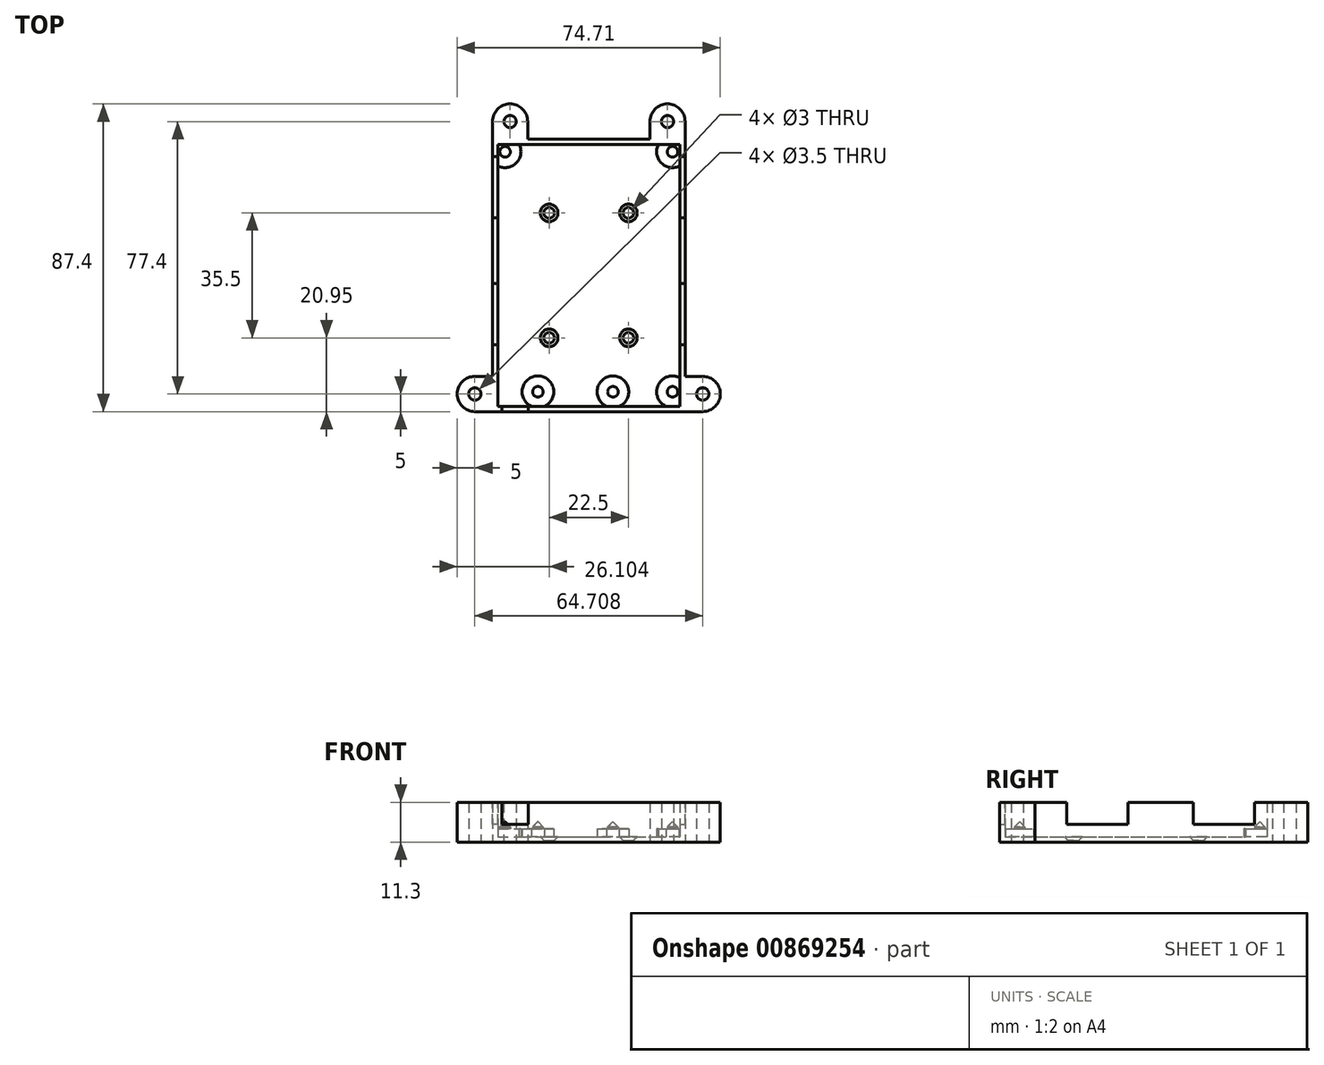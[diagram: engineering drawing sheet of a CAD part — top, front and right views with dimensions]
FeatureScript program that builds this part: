
annotation { "Feature Type Name" : "Feature", "Feature Type Description" : "" }
export const myFeature = defineFeature(function(context is Context, id is Id, definition is map)
    precondition{}
    {
        {
            var Q0;
            Q0=qCreatedBy(makeId("Top.planeOp"),FACE);
            var sketch = newSketch(context, id + "F0", { "sketchPlane" : qUnion([Q0])});
            skLineSegment(sketch, "E0.bottom", {"start": v(0, 0) * mm, "end": v(51.3, 0) * mm});
            skLineSegment(sketch, "E0.top", {"start": v(0, 74) * mm, "end": v(51.3, 74) * mm});
            skLineSegment(sketch, "E0.left", {"start": v(0, 0) * mm, "end": v(0, 74) * mm});
            skLineSegment(sketch, "E0.right", {"start": v(51.3, 0) * mm, "end": v(51.3, 74) * mm});
            skLineSegment(sketch, "E1.bottom", {"start": v(0, 69) * mm, "end": v(16.7, 69) * mm, "construction": true});
            skLineSegment(sketch, "E1.top", {"start": v(0, 55) * mm, "end": v(16.7, 55) * mm, "construction": true});
            skLineSegment(sketch, "E1.left", {"start": v(0, 69) * mm, "end": v(0, 55) * mm, "construction": true});
            skLineSegment(sketch, "E1.right", {"start": v(16.7, 69) * mm, "end": v(16.7, 55) * mm, "construction": true});
            skLineSegment(sketch, "E2.bottom", {"start": v(0, 33) * mm, "end": v(16.7, 33) * mm, "construction": true});
            skLineSegment(sketch, "E2.top", {"start": v(0, 19) * mm, "end": v(16.7, 19) * mm, "construction": true});
            skLineSegment(sketch, "E2.left", {"start": v(0, 33) * mm, "end": v(0, 19) * mm, "construction": true});
            skLineSegment(sketch, "E2.right", {"start": v(16.7, 33) * mm, "end": v(16.7, 19) * mm, "construction": true});
            skLineSegment(sketch, "E3.bottom", {"start": v(51.3, 69) * mm, "end": v(34.6, 69) * mm, "construction": true});
            skLineSegment(sketch, "E3.top", {"start": v(51.3, 55) * mm, "end": v(34.6, 55) * mm, "construction": true});
            skLineSegment(sketch, "E3.left", {"start": v(51.3, 69) * mm, "end": v(51.3, 55) * mm, "construction": true});
            skLineSegment(sketch, "E3.right", {"start": v(34.6, 69) * mm, "end": v(34.6, 55) * mm, "construction": true});
            skLineSegment(sketch, "E4.bottom", {"start": v(51.3, 33) * mm, "end": v(34.6, 33) * mm, "construction": true});
            skLineSegment(sketch, "E4.top", {"start": v(51.3, 19) * mm, "end": v(34.6, 19) * mm, "construction": true});
            skLineSegment(sketch, "E4.left", {"start": v(51.3, 33) * mm, "end": v(51.3, 19) * mm, "construction": true});
            skLineSegment(sketch, "E4.right", {"start": v(34.6, 33) * mm, "end": v(34.6, 19) * mm, "construction": true});
            skCircle(sketch, "E5", {"center": v(11.21, 3.92) * mm, "radius": 1.6 * mm});
            skCircle(sketch, "E6", {"center": v(32.51, 3.92) * mm, "radius": 1.6 * mm});
            skCircle(sketch, "E7", {"center": v(49.43, 3.92) * mm, "radius": 1.6 * mm});
            skCircle(sketch, "E8", {"center": v(49.43, 72.12) * mm, "radius": 1.6 * mm});
            skCircle(sketch, "E9", {"center": v(1.88, 72.12) * mm, "radius": 1.6 * mm});
            skLineSegment(sketch, "E10", {"start": v(1.88, 72.12) * mm, "end": v(49.43, 72.12) * mm, "construction": true});
            skSolve(sketch);
        }
        {
            var Q0;
            {var subQ10=sQuery(id+"F0.wireOp",EDGE,"E0.bottom");Q0=makeQuery(id+"F0.imprint","IMPRINT",FACE,{"disambiguationData":[TD([[makeQuery(id+"F0.imprint","IMPRINT",EDGE,{"derivedFrom":subQ10}),1.0]])]});}
            var sketch = newSketch(context, id + "F1", { "sketchPlane" : qUnion([Q0])});
            skLineSegment(sketch, "E11.0", {"start": v(-1.7, -1.7) * mm, "end": v(-1.7, 75.7) * mm});
            skLineSegment(sketch, "E11.1", {"start": v(-1.7, -1.7) * mm, "end": v(53, -1.7) * mm});
            skLineSegment(sketch, "E11.2", {"start": v(53, -1.7) * mm, "end": v(53, 75.7) * mm});
            skLineSegment(sketch, "E11.3", {"start": v(-1.7, 75.7) * mm, "end": v(53, 75.7) * mm});
            skSolve(sketch);
        }
        {
            var Q0;
            Q0=qSketchRegion(id+"F1",true);
            extrude(context, id + "F2", {"entities" : qUnion([Q0]), "depth" : 11.3 * mm, "offsetDistance" : 25 * mm});
        }
        {
            var Q0;
            Q0=makeQuery(id+"F2.opExtrude","CAP_FACE",FACE,{"disambiguationData":[OSD([sQuery(id+"F1.wireOp",EDGE,"E11.0"),sQuery(id+"F1.wireOp",EDGE,"E11.1"),sQuery(id+"F1.wireOp",EDGE,"E11.2"),sQuery(id+"F1.wireOp",EDGE,"E11.3")])],"isStart":false});
            shell(context, id + "F3", {"entities" : qUnion([Q0]), "thickness" : 1.5 * mm});
        }
        {
            var Q0;
            Q0=makeQuery(id+"F2.opExtrude","CAP_FACE",FACE,{"disambiguationData":[OSD([sQuery(id+"F1.wireOp",EDGE,"E11.0"),sQuery(id+"F1.wireOp",EDGE,"E11.1"),sQuery(id+"F1.wireOp",EDGE,"E11.2"),sQuery(id+"F1.wireOp",EDGE,"E11.3")])],"isStart":false});
            var sketch = newSketch(context, id + "F4", { "sketchPlane" : qUnion([Q0])});
            skLineSegment(sketch, "E12.0", {"start": v(16.7, 33) * mm, "end": v(16.7, 19) * mm, "construction": true});
            skLineSegment(sketch, "E13.0", {"start": v(34.6, 33) * mm, "end": v(34.6, 19) * mm, "construction": true});
            skLineSegment(sketch, "E14.0", {"start": v(16.7, 69) * mm, "end": v(16.7, 55) * mm, "construction": true});
            skLineSegment(sketch, "E15.0", {"start": v(34.6, 69) * mm, "end": v(34.6, 55) * mm, "construction": true});
            skLineSegment(sketch, "E16.0", {"start": v(0, 33) * mm, "end": v(16.7, 33) * mm, "construction": true});
            skLineSegment(sketch, "E17.0", {"start": v(0, 19) * mm, "end": v(16.7, 19) * mm, "construction": true});
            skLineSegment(sketch, "E18.0", {"start": v(51.3, 33) * mm, "end": v(34.6, 33) * mm, "construction": true});
            skLineSegment(sketch, "E19.0", {"start": v(51.3, 19) * mm, "end": v(34.6, 19) * mm, "construction": true});
            skLineSegment(sketch, "E20.0", {"start": v(51.3, 55) * mm, "end": v(34.6, 55) * mm, "construction": true});
            skLineSegment(sketch, "E21.0", {"start": v(51.3, 69) * mm, "end": v(34.6, 69) * mm, "construction": true});
            skLineSegment(sketch, "E22.0", {"start": v(0, 55) * mm, "end": v(16.7, 55) * mm, "construction": true});
            skLineSegment(sketch, "E23.0", {"start": v(0, 69) * mm, "end": v(16.7, 69) * mm, "construction": true});
            skLineSegment(sketch, "E24.0", {"start": v(0, 33) * mm, "end": v(0, 19) * mm});
            skLineSegment(sketch, "E25.0", {"start": v(51.3, 33) * mm, "end": v(51.3, 19) * mm});
            skLineSegment(sketch, "E26.0", {"start": v(0, 69) * mm, "end": v(0, 55) * mm});
            skLineSegment(sketch, "E27.0", {"start": v(51.3, 69) * mm, "end": v(51.3, 55) * mm});
            skLineSegment(sketch, "E28.0", {"start": v(-1.7, 17.3) * mm, "end": v(18.4, 17.3) * mm});
            skLineSegment(sketch, "E28.1", {"start": v(-1.7, 34.7) * mm, "end": v(-1.7, 17.3) * mm});
            skLineSegment(sketch, "E28.2", {"start": v(-1.7, 34.7) * mm, "end": v(18.4, 34.7) * mm});
            skLineSegment(sketch, "E28.3", {"start": v(18.4, 34.7) * mm, "end": v(18.4, 17.3) * mm});
            skLineSegment(sketch, "E29.0", {"start": v(53, 17.3) * mm, "end": v(32.9, 17.3) * mm});
            skLineSegment(sketch, "E29.1", {"start": v(53, 34.7) * mm, "end": v(53, 17.3) * mm});
            skLineSegment(sketch, "E29.2", {"start": v(53, 34.7) * mm, "end": v(32.9, 34.7) * mm});
            skLineSegment(sketch, "E29.3", {"start": v(32.9, 34.7) * mm, "end": v(32.9, 17.3) * mm});
            skLineSegment(sketch, "E30.0", {"start": v(-1.7, 53.3) * mm, "end": v(18.4, 53.3) * mm});
            skLineSegment(sketch, "E30.1", {"start": v(-1.7, 70.7) * mm, "end": v(-1.7, 53.3) * mm});
            skLineSegment(sketch, "E30.2", {"start": v(-1.7, 70.7) * mm, "end": v(18.4, 70.7) * mm});
            skLineSegment(sketch, "E30.3", {"start": v(18.4, 70.7) * mm, "end": v(18.4, 53.3) * mm});
            skLineSegment(sketch, "E31.0", {"start": v(53, 53.3) * mm, "end": v(32.9, 53.3) * mm});
            skLineSegment(sketch, "E31.1", {"start": v(53, 70.7) * mm, "end": v(53, 53.3) * mm});
            skLineSegment(sketch, "E31.2", {"start": v(53, 70.7) * mm, "end": v(32.9, 70.7) * mm});
            skLineSegment(sketch, "E31.3", {"start": v(32.9, 70.7) * mm, "end": v(32.9, 53.3) * mm});
            skSolve(sketch);
        }
        {
            var Q0;
            Q0=qSketchRegion(id+"F4",true);
            var Q1;
            Q1=makeQuery(id+"F3.opShell","OFFSET_FACE",FACE,{"disambiguationData":[OSD([sQuery(id+"F1.wireOp",EDGE,"E11.0"),sQuery(id+"F1.wireOp",EDGE,"E11.1"),sQuery(id+"F1.wireOp",EDGE,"E11.2"),sQuery(id+"F1.wireOp",EDGE,"E11.3")])]});
            extrude(context, id + "F5", {"entities" : qUnion([Q0]), "operationType" : NewBodyOperationType.REMOVE, "endBound" : BoundingType.UP_TO_SURFACE, "oppositeDirection" : true, "depth" : 25 * mm, "endBoundEntityFace" : qUnion([Q1]), "hasOffset" : true, "offsetDistance" : 3.5 * mm});
        }
        {
            var Q0;
            Q0=makeQuery(id+"F3.opShell","OFFSET_FACE",FACE,{"disambiguationData":[OSD([sQuery(id+"F1.wireOp",EDGE,"E11.0"),sQuery(id+"F1.wireOp",EDGE,"E11.1"),sQuery(id+"F1.wireOp",EDGE,"E11.2"),sQuery(id+"F1.wireOp",EDGE,"E11.3")])]});
            var sketch = newSketch(context, id + "F6", { "sketchPlane" : qUnion([Q0])});
            skCircle(sketch, "E32.0", {"center": v(1.88, 72.12) * mm, "radius": 1.5 * mm, "construction": true});
            skCircle(sketch, "E33.0", {"center": v(49.43, 72.12) * mm, "radius": 1.5 * mm, "construction": true});
            skCircle(sketch, "E34.0", {"center": v(11.21, 3.92) * mm, "radius": 1.5 * mm, "construction": true});
            skCircle(sketch, "E35.0", {"center": v(32.51, 3.92) * mm, "radius": 1.5 * mm, "construction": true});
            skCircle(sketch, "E36.0", {"center": v(49.43, 3.92) * mm, "radius": 1.5 * mm, "construction": true});
            skArc(sketch, "E37.0", {"start": v(-1.7, 69.4) * mm, "mid": v(6.38, 72.12) * mm, "end": v(-1.7, 74.85) * mm});
            skArc(sketch, "E38.0", {"start": v(53, 74.85) * mm, "mid": v(44.93, 72.12) * mm, "end": v(53, 69.4) * mm});
            skCircle(sketch, "E39.0", {"center": v(11.21, 3.92) * mm, "radius": 4.5 * mm});
            skCircle(sketch, "E40.0", {"center": v(32.51, 3.92) * mm, "radius": 4.5 * mm});
            skArc(sketch, "E41.0", {"start": v(53, 6.65) * mm, "mid": v(44.93, 3.92) * mm, "end": v(53, 1.2) * mm});
            skLineSegment(sketch, "E42.0", {"start": v(53, 1.2) * mm, "end": v(53, 6.65) * mm});
            skLineSegment(sketch, "E43.0", {"start": v(-1.7, 69.4) * mm, "end": v(-1.7, 74.85) * mm});
            skPoint(sketch, "E44.orphan", {"position": v(53, -1.7) * mm});
            skLineSegment(sketch, "E45.trimOffspring", {"start": v(53, 69.4) * mm, "end": v(53, 74.85) * mm});
            skPoint(sketch, "E46.orphan", {"position": v(-1.7, -1.7) * mm});
            skPoint(sketch, "E47.0.start.orphan", {"position": v(-1.7, 75.7) * mm});
            skPoint(sketch, "E48.orphan", {"position": v(53, 75.7) * mm});
            skSolve(sketch);
        }
        {
            var Q0;
            Q0=qSketchRegion(id+"F6",true);
            var Q1;
            Q1=makeQuery(id+"F5.boolean.opBoolean","COPY",FACE,{"derivedFrom":makeQuery(id+"F5.opExtrude","CAP_FACE",FACE,{"disambiguationData":[OSD([sQuery(id+"F4.wireOp",EDGE,"E28.0"),sQuery(id+"F4.wireOp",EDGE,"E28.1"),sQuery(id+"F4.wireOp",EDGE,"E28.2"),sQuery(id+"F4.wireOp",EDGE,"E28.3")])],"isStart":false})});
            extrude(context, id + "F7", {"entities" : qUnion([Q0]), "operationType" : NewBodyOperationType.ADD, "endBound" : BoundingType.UP_TO_SURFACE, "depth" : 25 * mm, "endBoundEntityFace" : qUnion([Q1]), "hasOffset" : true, "offsetDistance" : 1.2 * mm});
        }
        {
            var Q0;
            Q0=makeQuery(id+"F2.opExtrude","CAP_FACE",FACE,{"disambiguationData":[OSD([sQuery(id+"F1.wireOp",EDGE,"E11.0"),sQuery(id+"F1.wireOp",EDGE,"E11.1"),sQuery(id+"F1.wireOp",EDGE,"E11.2"),sQuery(id+"F1.wireOp",EDGE,"E11.3")])],"isStart":true});
            var sketch = newSketch(context, id + "F8", { "sketchPlane" : qUnion([Q0])});
            skLineSegment(sketch, "E49", {"start": v(25.65, -75.7) * mm, "end": v(25.65, 1.7) * mm, "construction": true});
            skLineSegment(sketch, "E50", {"start": v(-1.7, -37) * mm, "end": v(53, -37) * mm, "construction": true});
            skCircle(sketch, "E51", {"center": v(14.4, -54.75) * mm, "radius": 1.5 * mm});
            skCircle(sketch, "E52", {"center": v(14.4, -19.25) * mm, "radius": 1.5 * mm});
            skCircle(sketch, "E53", {"center": v(36.9, -19.25) * mm, "radius": 1.5 * mm});
            skCircle(sketch, "E54", {"center": v(36.9, -54.75) * mm, "radius": 1.5 * mm});
            skLineSegment(sketch, "E55", {"start": v(36.9, -54.75) * mm, "end": v(36.9, -19.25) * mm, "construction": true});
            skLineSegment(sketch, "E56", {"start": v(14.4, -19.25) * mm, "end": v(36.9, -19.25) * mm, "construction": true});
            skLineSegment(sketch, "E57", {"start": v(14.4, -54.75) * mm, "end": v(14.4, -19.25) * mm, "construction": true});
            skLineSegment(sketch, "E58", {"start": v(14.4, -54.75) * mm, "end": v(36.9, -54.75) * mm, "construction": true});
            skLineSegment(sketch, "E59", {"start": v(14.4, -37) * mm, "end": v(36.9, -37) * mm, "construction": true});
            skLineSegment(sketch, "E60", {"start": v(25.65, -19.25) * mm, "end": v(25.65, -54.75) * mm, "construction": true});
            skSolve(sketch);
        }
        {
            var Q0;
            Q0=qSketchRegion(id+"F8",true);
            extrude(context, id + "F9", {"entities" : qUnion([Q0]), "operationType" : NewBodyOperationType.REMOVE, "endBound" : BoundingType.THROUGH_ALL, "oppositeDirection" : true, "depth" : 25 * mm, "offsetDistance" : 25 * mm});
        }
        {
            var Q0;
            {var subQ0=sQuery(id+"F1.wireOp",EDGE,"E11.3");var subQ1=sQuery(id+"F1.wireOp",EDGE,"E11.2");var subQ2=sQuery(id+"F1.wireOp",EDGE,"E11.1");var subQ3=sQuery(id+"F1.wireOp",EDGE,"E11.0");Q0=makeQuery(id+"F9.boolean.opBoolean","INTERSECT",EDGE,{"derivedFrom":[makeQuery(id+"F7.boolean.opBoolean","SPLIT",FACE,{"disambiguationData":[TD([makeQuery(id+"F3.opShell","OFFSET_FACE",FACE,{"disambiguationData":[OSD([subQ3])]}),makeQuery(id+"F3.opShell","OFFSET_FACE",FACE,{"disambiguationData":[OSD([subQ2])]}),makeQuery(id+"F3.opShell","OFFSET_FACE",FACE,{"disambiguationData":[OSD([subQ1])]}),makeQuery(id+"F3.opShell","OFFSET_FACE",FACE,{"disambiguationData":[OSD([subQ0])]}),makeQuery(id+"F7.opExtrude","SWEPT_FACE",FACE,{"disambiguationData":[OSD([sQuery(id+"F6.wireOp",EDGE,"E37.0")])]}),makeQuery(id+"F7.opExtrude","SWEPT_FACE",FACE,{"disambiguationData":[OSD([sQuery(id+"F6.wireOp",EDGE,"E38.0")])]}),makeQuery(id+"F7.opExtrude","SWEPT_FACE",FACE,{"disambiguationData":[OSD([sQuery(id+"F6.wireOp",EDGE,"E39.0")])]}),makeQuery(id+"F7.opExtrude","SWEPT_FACE",FACE,{"disambiguationData":[OSD([sQuery(id+"F6.wireOp",EDGE,"E40.0")])]}),makeQuery(id+"F7.opExtrude","SWEPT_FACE",FACE,{"disambiguationData":[OSD([sQuery(id+"F6.wireOp",EDGE,"E41.0")])]})])],"derivedFrom":makeQuery(id+"F3.opShell","OFFSET_FACE",FACE,{"disambiguationData":[OSD([subQ3,subQ2,subQ1,subQ0])]})}),makeQuery(id+"F9.opExtrude","SWEPT_FACE",FACE,{"disambiguationData":[OSD([sQuery(id+"F8.wireOp",EDGE,"E54")])]})]});}
            var Q1;
            {var subQ0=sQuery(id+"F1.wireOp",EDGE,"E11.3");var subQ1=sQuery(id+"F1.wireOp",EDGE,"E11.2");var subQ2=sQuery(id+"F1.wireOp",EDGE,"E11.1");var subQ3=sQuery(id+"F1.wireOp",EDGE,"E11.0");Q1=makeQuery(id+"F9.boolean.opBoolean","INTERSECT",EDGE,{"derivedFrom":[makeQuery(id+"F7.boolean.opBoolean","SPLIT",FACE,{"disambiguationData":[TD([makeQuery(id+"F3.opShell","OFFSET_FACE",FACE,{"disambiguationData":[OSD([subQ3])]}),makeQuery(id+"F3.opShell","OFFSET_FACE",FACE,{"disambiguationData":[OSD([subQ2])]}),makeQuery(id+"F3.opShell","OFFSET_FACE",FACE,{"disambiguationData":[OSD([subQ1])]}),makeQuery(id+"F3.opShell","OFFSET_FACE",FACE,{"disambiguationData":[OSD([subQ0])]}),makeQuery(id+"F7.opExtrude","SWEPT_FACE",FACE,{"disambiguationData":[OSD([sQuery(id+"F6.wireOp",EDGE,"E37.0")])]}),makeQuery(id+"F7.opExtrude","SWEPT_FACE",FACE,{"disambiguationData":[OSD([sQuery(id+"F6.wireOp",EDGE,"E38.0")])]}),makeQuery(id+"F7.opExtrude","SWEPT_FACE",FACE,{"disambiguationData":[OSD([sQuery(id+"F6.wireOp",EDGE,"E39.0")])]}),makeQuery(id+"F7.opExtrude","SWEPT_FACE",FACE,{"disambiguationData":[OSD([sQuery(id+"F6.wireOp",EDGE,"E40.0")])]}),makeQuery(id+"F7.opExtrude","SWEPT_FACE",FACE,{"disambiguationData":[OSD([sQuery(id+"F6.wireOp",EDGE,"E41.0")])]})])],"derivedFrom":makeQuery(id+"F3.opShell","OFFSET_FACE",FACE,{"disambiguationData":[OSD([subQ3,subQ2,subQ1,subQ0])]})}),makeQuery(id+"F9.opExtrude","SWEPT_FACE",FACE,{"disambiguationData":[OSD([sQuery(id+"F8.wireOp",EDGE,"E51")])]})]});}
            var Q2;
            {var subQ0=sQuery(id+"F1.wireOp",EDGE,"E11.3");var subQ1=sQuery(id+"F1.wireOp",EDGE,"E11.2");var subQ2=sQuery(id+"F1.wireOp",EDGE,"E11.1");var subQ3=sQuery(id+"F1.wireOp",EDGE,"E11.0");Q2=makeQuery(id+"F9.boolean.opBoolean","INTERSECT",EDGE,{"derivedFrom":[makeQuery(id+"F7.boolean.opBoolean","SPLIT",FACE,{"disambiguationData":[TD([makeQuery(id+"F3.opShell","OFFSET_FACE",FACE,{"disambiguationData":[OSD([subQ3])]}),makeQuery(id+"F3.opShell","OFFSET_FACE",FACE,{"disambiguationData":[OSD([subQ2])]}),makeQuery(id+"F3.opShell","OFFSET_FACE",FACE,{"disambiguationData":[OSD([subQ1])]}),makeQuery(id+"F3.opShell","OFFSET_FACE",FACE,{"disambiguationData":[OSD([subQ0])]}),makeQuery(id+"F7.opExtrude","SWEPT_FACE",FACE,{"disambiguationData":[OSD([sQuery(id+"F6.wireOp",EDGE,"E37.0")])]}),makeQuery(id+"F7.opExtrude","SWEPT_FACE",FACE,{"disambiguationData":[OSD([sQuery(id+"F6.wireOp",EDGE,"E38.0")])]}),makeQuery(id+"F7.opExtrude","SWEPT_FACE",FACE,{"disambiguationData":[OSD([sQuery(id+"F6.wireOp",EDGE,"E39.0")])]}),makeQuery(id+"F7.opExtrude","SWEPT_FACE",FACE,{"disambiguationData":[OSD([sQuery(id+"F6.wireOp",EDGE,"E40.0")])]}),makeQuery(id+"F7.opExtrude","SWEPT_FACE",FACE,{"disambiguationData":[OSD([sQuery(id+"F6.wireOp",EDGE,"E41.0")])]})])],"derivedFrom":makeQuery(id+"F3.opShell","OFFSET_FACE",FACE,{"disambiguationData":[OSD([subQ3,subQ2,subQ1,subQ0])]})}),makeQuery(id+"F9.opExtrude","SWEPT_FACE",FACE,{"disambiguationData":[OSD([sQuery(id+"F8.wireOp",EDGE,"E53")])]})]});}
            var Q3;
            {var subQ0=sQuery(id+"F1.wireOp",EDGE,"E11.3");var subQ1=sQuery(id+"F1.wireOp",EDGE,"E11.2");var subQ2=sQuery(id+"F1.wireOp",EDGE,"E11.1");var subQ3=sQuery(id+"F1.wireOp",EDGE,"E11.0");Q3=makeQuery(id+"F9.boolean.opBoolean","INTERSECT",EDGE,{"derivedFrom":[makeQuery(id+"F7.boolean.opBoolean","SPLIT",FACE,{"disambiguationData":[TD([makeQuery(id+"F3.opShell","OFFSET_FACE",FACE,{"disambiguationData":[OSD([subQ3])]}),makeQuery(id+"F3.opShell","OFFSET_FACE",FACE,{"disambiguationData":[OSD([subQ2])]}),makeQuery(id+"F3.opShell","OFFSET_FACE",FACE,{"disambiguationData":[OSD([subQ1])]}),makeQuery(id+"F3.opShell","OFFSET_FACE",FACE,{"disambiguationData":[OSD([subQ0])]}),makeQuery(id+"F7.opExtrude","SWEPT_FACE",FACE,{"disambiguationData":[OSD([sQuery(id+"F6.wireOp",EDGE,"E37.0")])]}),makeQuery(id+"F7.opExtrude","SWEPT_FACE",FACE,{"disambiguationData":[OSD([sQuery(id+"F6.wireOp",EDGE,"E38.0")])]}),makeQuery(id+"F7.opExtrude","SWEPT_FACE",FACE,{"disambiguationData":[OSD([sQuery(id+"F6.wireOp",EDGE,"E39.0")])]}),makeQuery(id+"F7.opExtrude","SWEPT_FACE",FACE,{"disambiguationData":[OSD([sQuery(id+"F6.wireOp",EDGE,"E40.0")])]}),makeQuery(id+"F7.opExtrude","SWEPT_FACE",FACE,{"disambiguationData":[OSD([sQuery(id+"F6.wireOp",EDGE,"E41.0")])]})])],"derivedFrom":makeQuery(id+"F3.opShell","OFFSET_FACE",FACE,{"disambiguationData":[OSD([subQ3,subQ2,subQ1,subQ0])]})}),makeQuery(id+"F9.opExtrude","SWEPT_FACE",FACE,{"disambiguationData":[OSD([sQuery(id+"F8.wireOp",EDGE,"E52")])]})]});}
            chamfer(context, id + "F10", {"entities" : qUnion([Q0, Q1, Q2, Q3]), "width" : 1 * mm, "tangentPropagation" : true});
        }
        {
            var Q0;
            Q0=makeQuery(id+"F2.opExtrude","CAP_FACE",FACE,{"disambiguationData":[OSD([sQuery(id+"F1.wireOp",EDGE,"E11.0"),sQuery(id+"F1.wireOp",EDGE,"E11.1"),sQuery(id+"F1.wireOp",EDGE,"E11.2"),sQuery(id+"F1.wireOp",EDGE,"E11.3")])],"isStart":true});
            var sketch = newSketch(context, id + "F11", { "sketchPlane" : qUnion([Q0])});
            skArc(sketch, "E61", {"start": v(-6.7, 1.7) * mm, "mid": v(-11.7, -3.3) * mm, "end": v(-6.7, -8.3) * mm});
            skArc(sketch, "E62", {"start": v(-1.7, -80.7) * mm, "mid": v(3.3, -85.7) * mm, "end": v(8.3, -80.7) * mm});
            skLineSegment(sketch, "E63", {"start": v(-1.7, 1.7) * mm, "end": v(-6.7, 1.7) * mm});
            skLineSegment(sketch, "E64", {"start": v(-6.7, -8.3) * mm, "end": v(-1.7, -8.3) * mm});
            skLineSegment(sketch, "E65", {"start": v(25.65, 1.7) * mm, "end": v(25.65, -75.7) * mm, "construction": true});
            skLineSegment(sketch, "E66", {"start": v(-1.7, 1.7) * mm, "end": v(-1.7, -8.3) * mm});
            skLineSegment(sketch, "E67", {"start": v(-1.7, -75.7) * mm, "end": v(-1.7, -80.7) * mm});
            skLineSegment(sketch, "E68", {"start": v(8.3, -80.7) * mm, "end": v(8.3, -75.7) * mm});
            skLineSegment(sketch, "E69", {"start": v(-1.7, -75.7) * mm, "end": v(8.3, -75.7) * mm});
            skLineSegment(sketch, "E70.MirrorCS", {"start": v(58, -8.3) * mm, "end": v(53, -8.3) * mm});
            skLineSegment(sketch, "E71.MirrorCS", {"start": v(43, -80.7) * mm, "end": v(43, -75.7) * mm});
            skLineSegment(sketch, "E72.MirrorCS", {"start": v(53, 1.7) * mm, "end": v(58, 1.7) * mm});
            skLineSegment(sketch, "E73.MirrorCS", {"start": v(53, -75.7) * mm, "end": v(53, -80.7) * mm});
            skLineSegment(sketch, "E74.MirrorCS", {"start": v(53, 1.7) * mm, "end": v(53, -8.3) * mm});
            skLineSegment(sketch, "E75.MirrorCS", {"start": v(53, -75.7) * mm, "end": v(43, -75.7) * mm});
            skArc(sketch, "E76.MirrorCS", {"start": v(53, -80.7) * mm, "mid": v(48, -85.7) * mm, "end": v(43, -80.7) * mm});
            skArc(sketch, "E77.MirrorCS", {"start": v(58, 1.7) * mm, "mid": v(63, -3.3) * mm, "end": v(58, -8.3) * mm});
            skCircle(sketch, "E78", {"center": v(-6.7, -3.3) * mm, "radius": 1.75 * mm});
            skCircle(sketch, "E79", {"center": v(58, -3.3) * mm, "radius": 1.75 * mm});
            skCircle(sketch, "E80", {"center": v(48, -80.7) * mm, "radius": 1.75 * mm});
            skCircle(sketch, "E81", {"center": v(3.3, -80.7) * mm, "radius": 1.75 * mm});
            skSolve(sketch);
        }
        {
            var Q0;
            Q0=qSketchRegion(id+"F11",true);
            var Q1;
            {var subQ0=sQuery(id+"F1.wireOp",EDGE,"E11.0");var subQ1=sQuery(id+"F1.wireOp",EDGE,"E11.2");var subQ2=sQuery(id+"F1.wireOp",EDGE,"E11.3");Q1=makeQuery(id+"F5.boolean.opBoolean","SPLIT",FACE,{"disambiguationData":[TD([makeQuery(id+"F2.opExtrude","SWEPT_FACE",FACE,{"disambiguationData":[OSD([subQ2])]})])],"derivedFrom":makeQuery(id+"F2.opExtrude","CAP_FACE",FACE,{"disambiguationData":[OSD([subQ0,sQuery(id+"F1.wireOp",EDGE,"E11.1"),subQ1,subQ2])],"isStart":false})});}
            extrude(context, id + "F12", {"entities" : qUnion([Q0]), "operationType" : NewBodyOperationType.ADD, "endBound" : BoundingType.UP_TO_SURFACE, "oppositeDirection" : true, "depth" : 25 * mm, "endBoundEntityFace" : qUnion([Q1]), "offsetDistance" : 25 * mm});
        }
        {
            var Q0;
            Q0=makeQuery(id+"F7.opExtrude","CAP_FACE",FACE,{"disambiguationData":[OSD([sQuery(id+"F6.wireOp",EDGE,"E39.0")])],"isStart":false});
            var sketch = newSketch(context, id + "F13", { "sketchPlane" : qUnion([Q0])});
            skCircle(sketch, "E82.0", {"center": v(49.43, 3.92) * mm, "radius": 1.5 * mm});
            skCircle(sketch, "E83.0", {"center": v(32.51, 3.92) * mm, "radius": 1.5 * mm});
            skCircle(sketch, "E84.0", {"center": v(11.21, 3.92) * mm, "radius": 1.5 * mm});
            skCircle(sketch, "E85.0", {"center": v(49.43, 72.12) * mm, "radius": 1.5 * mm});
            skCircle(sketch, "E86.0", {"center": v(1.88, 72.12) * mm, "radius": 1.5 * mm});
            skSolve(sketch);
        }
        {
            var Q0;
            Q0=qSketchRegion(id+"F13",true);
            extrude(context, id + "F14", {"entities" : qUnion([Q0]), "operationType" : NewBodyOperationType.ADD, "depth" : 2 * mm, "offsetDistance" : 25 * mm});
        }
        {
            var Q0;
            Q0=makeQuery(id+"F14.opExtrude","CAP_FACE",FACE,{"disambiguationData":[OSD([sQuery(id+"F13.wireOp",EDGE,"E82.0")])],"isStart":false});
            var Q1;
            Q1=makeQuery(id+"F14.opExtrude","CAP_EDGE",EDGE,{"disambiguationData":[OSD([sQuery(id+"F13.wireOp",EDGE,"E83.0")])],"isStart":false});
            var Q2;
            Q2=makeQuery(id+"F14.opExtrude","CAP_FACE",FACE,{"disambiguationData":[OSD([sQuery(id+"F13.wireOp",EDGE,"E84.0")])],"isStart":false});
            var Q3;
            Q3=makeQuery(id+"F14.opExtrude","CAP_FACE",FACE,{"disambiguationData":[OSD([sQuery(id+"F13.wireOp",EDGE,"E85.0")])],"isStart":false});
            var Q4;
            Q4=makeQuery(id+"F14.opExtrude","CAP_EDGE",EDGE,{"disambiguationData":[OSD([sQuery(id+"F13.wireOp",EDGE,"E86.0")])],"isStart":false});
            chamfer(context, id + "F15", {"entities" : qUnion([Q0, Q1, Q2, Q3, Q4]), "width" : 1.5 * mm, "tangentPropagation" : true});
        }
        {
            var Q0;
            {var subQ0=sQuery(id+"F1.wireOp",EDGE,"E11.0");var subQ1=sQuery(id+"F1.wireOp",EDGE,"E11.2");var subQ2=sQuery(id+"F1.wireOp",EDGE,"E11.1");Q0=makeQuery(id+"F12.boolean.opBoolean","MERGE",FACE,{"derivedFrom":[makeQuery(id+"F5.boolean.opBoolean","SPLIT",FACE,{"disambiguationData":[TD([makeQuery(id+"F2.opExtrude","SWEPT_FACE",FACE,{"disambiguationData":[OSD([subQ2])]})])],"derivedFrom":makeQuery(id+"F2.opExtrude","CAP_FACE",FACE,{"disambiguationData":[OSD([subQ0,subQ2,subQ1,sQuery(id+"F1.wireOp",EDGE,"E11.3")])],"isStart":false})}),makeQuery(id+"F12.opExtrude","CAP_FACE",FACE,{"disambiguationData":[OSD([sQuery(id+"F11.wireOp",EDGE,"E61"),sQuery(id+"F11.wireOp",EDGE,"E63"),sQuery(id+"F11.wireOp",EDGE,"E64"),sQuery(id+"F11.wireOp",EDGE,"E66")])],"isStart":false}),makeQuery(id+"F12.opExtrude","CAP_FACE",FACE,{"disambiguationData":[OSD([sQuery(id+"F11.wireOp",EDGE,"E70.MirrorCS"),sQuery(id+"F11.wireOp",EDGE,"E72.MirrorCS"),sQuery(id+"F11.wireOp",EDGE,"E74.MirrorCS"),sQuery(id+"F11.wireOp",EDGE,"E77.MirrorCS")])],"isStart":false})]});}
            var sketch = newSketch(context, id + "F16", { "sketchPlane" : qUnion([Q0])});
            skLineSegment(sketch, "E87.bottom", {"start": v(1, -0.2) * mm, "end": v(8.5, -0.2) * mm});
            skLineSegment(sketch, "E87.top", {"start": v(1, -1.7) * mm, "end": v(8.5, -1.7) * mm});
            skLineSegment(sketch, "E87.left", {"start": v(1, -0.2) * mm, "end": v(1, -1.7) * mm});
            skLineSegment(sketch, "E87.right", {"start": v(8.5, -0.2) * mm, "end": v(8.5, -1.7) * mm});
            skSolve(sketch);
        }
        {
            var Q0;
            Q0=qSketchRegion(id+"F16",true);
            var Q1;
            Q1=makeQuery(id+"F5.boolean.opBoolean","COPY",FACE,{"derivedFrom":makeQuery(id+"F5.opExtrude","CAP_FACE",FACE,{"disambiguationData":[OSD([sQuery(id+"F4.wireOp",EDGE,"E28.0"),sQuery(id+"F4.wireOp",EDGE,"E28.1"),sQuery(id+"F4.wireOp",EDGE,"E28.2"),sQuery(id+"F4.wireOp",EDGE,"E28.3")])],"isStart":false})});
            extrude(context, id + "F17", {"entities" : qUnion([Q0]), "operationType" : NewBodyOperationType.REMOVE, "endBound" : BoundingType.UP_TO_SURFACE, "oppositeDirection" : true, "depth" : 25 * mm, "endBoundEntityFace" : qUnion([Q1]), "offsetDistance" : 1.2 * mm});
        }
    });
